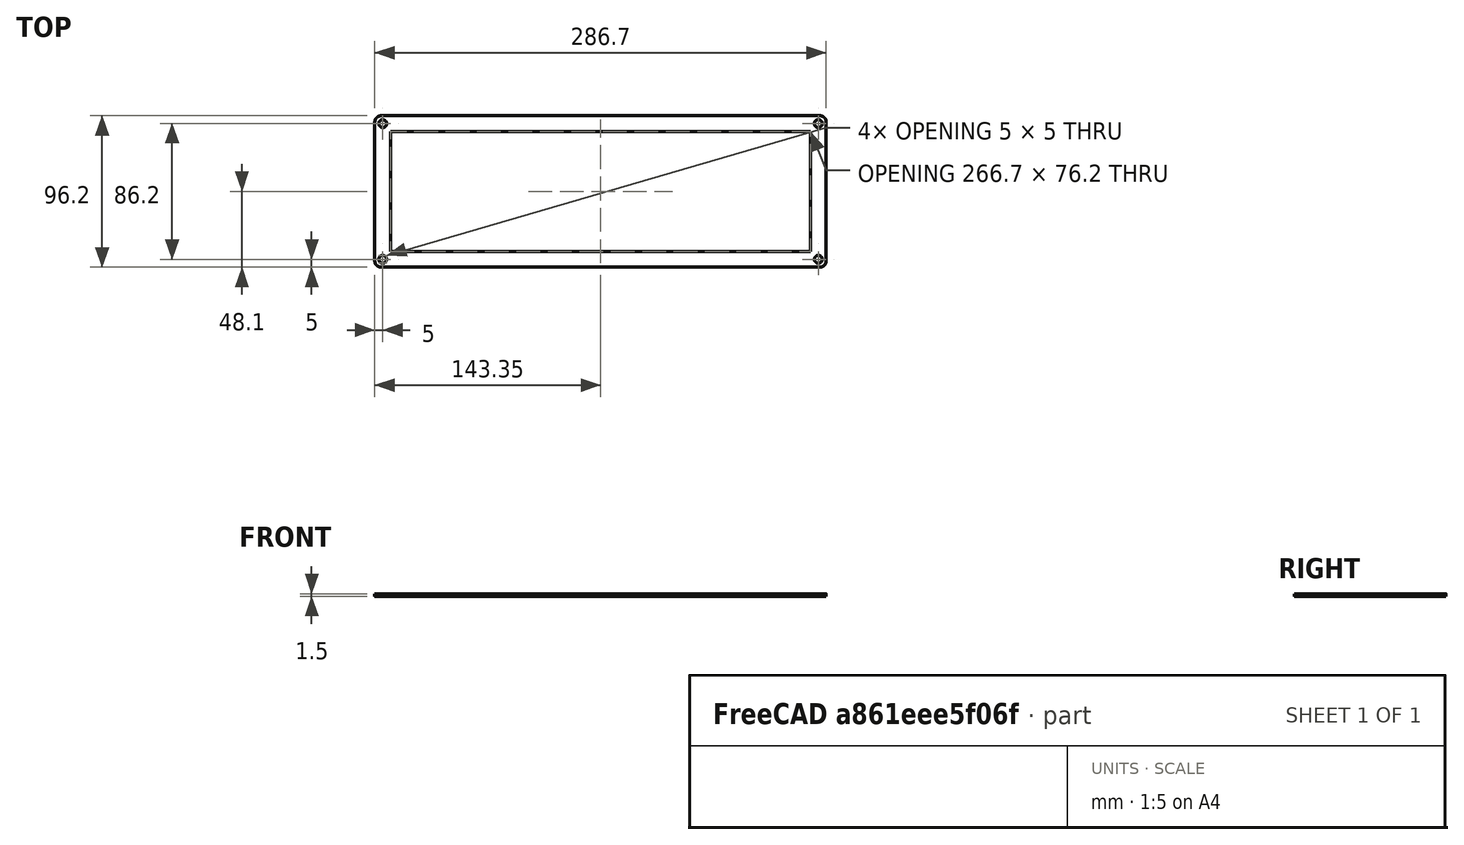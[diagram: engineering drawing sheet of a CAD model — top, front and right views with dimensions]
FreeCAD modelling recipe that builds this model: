
FCSTD DOCUMENT  (FreeCAD 0.16R6703 (Git))
Label: C
License: All rights reserved
LicenseURL: http://en.wikipedia.org/wiki/All_rights_reserved
objects: Part::Feature×6, Part::Extrusion×2, Part::MultiFuse×1, Part::Cut×1
note: 10 computed .brp shape members not serialized (recipe doc carries the construction recipe); baked Part::Feature solids carry a one-line shape summary decoded from their .brp

FEATURE [Part::Feature] Face
  shape: bbox 286.7 x 96.2 x 2e-07 mm, 1 faces, 0 solids (baked)
FEATURE [Part::Feature] Face001
  shape: bbox 266.7 x 76.2 x 2e-07 mm, 1 faces, 0 solids (baked)
FEATURE [Part::Feature] Face002 .. Face005  x4 (patterned run collapsed; names and placements below)
  shape: bbox 5 x 5 x 2e-07 mm, 1 faces, 0 solids (baked)
FEATURE [Part::MultiFuse] Fusion
  Shapes = -> [Face001,Face002,Face003,Face005,Face004]
FEATURE [Part::Extrusion] Extrude
  Base = -> Face
  Dir = (0,0,1.5)
  Solid = true
FEATURE [Part::Extrusion] Extrude001
  Base = -> Fusion
  Dir = (0,0,1.5)
  Solid = true
FEATURE [Part::Cut] Cut
  Base = -> Extrude
  Tool = -> Extrude001
